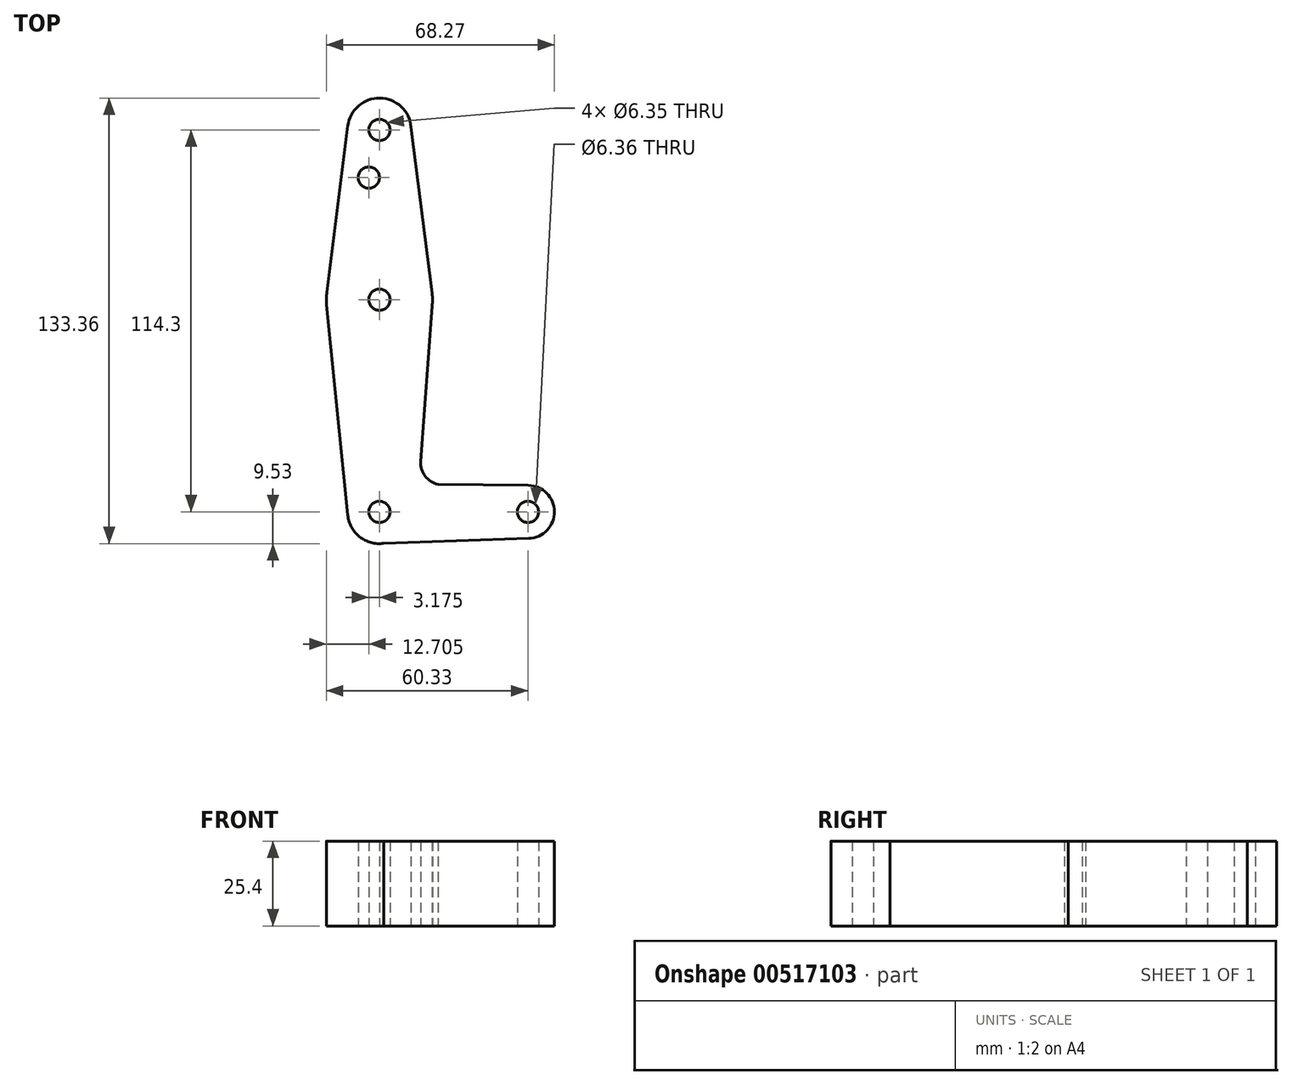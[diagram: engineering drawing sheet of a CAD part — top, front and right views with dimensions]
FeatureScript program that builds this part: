
annotation { "Feature Type Name" : "Feature", "Feature Type Description" : "" }
export const myFeature = defineFeature(function(context is Context, id is Id, definition is map)
    precondition{}
    {
        {
            var Q0;
            Q0=qCreatedBy(makeId("Top.planeOp"),FACE);
            var sketch = newSketch(context, id + "F0", { "sketchPlane" : qUnion([Q0])});
            skCircle(sketch, "E0", {"center": v(0, 0) * mm, "radius": 15.88 * mm});
            skCircle(sketch, "E1", {"center": v(0, 50.8) * mm, "radius": 3.18 * mm});
            skCircle(sketch, "E2", {"center": v(0, 50.8) * mm, "radius": 9.53 * mm});
            skCircle(sketch, "E3", {"center": v(0, 0) * mm, "radius": 3.18 * mm});
            skCircle(sketch, "E4", {"center": v(0, -63.5) * mm, "radius": 3.18 * mm});
            skCircle(sketch, "E5", {"center": v(0, -63.5) * mm, "radius": 9.53 * mm});
            skCircle(sketch, "E6", {"center": v(-3.18, 36.53) * mm, "radius": 3.18 * mm});
            skCircle(sketch, "E7", {"center": v(44.45, -63.5) * mm, "radius": 3.18 * mm});
            skCircle(sketch, "E8", {"center": v(44.45, -63.5) * mm, "radius": 7.94 * mm});
            skLineSegment(sketch, "E9", {"start": v(-9.47, -64.48) * mm, "end": v(-15.95, 0) * mm});
            skLineSegment(sketch, "E10", {"start": v(-15.71, 2.25) * mm, "end": v(-9.45, 52) * mm});
            skLineSegment(sketch, "E11", {"start": v(9.4, 52.32) * mm, "end": v(15.75, 1.99) * mm});
            skLineSegment(sketch, "E12", {"start": v(15.75, -1.99) * mm, "end": v(12.38, -48.36) * mm});
            skArc(sketch, "E13", {"start": v(12.38, -48.36) * mm, "mid": v(13.67, -52.79) * mm, "end": v(17.56, -55.27) * mm});
            skLineSegment(sketch, "E14", {"start": v(17.56, -55.27) * mm, "end": v(44.54, -55.56) * mm});
            skLineSegment(sketch, "E15", {"start": v(44.72, -71.43) * mm, "end": v(0, -72.98) * mm});
            skSolve(sketch);
        }
        {
            var Q0;
            Q0 = qSketchRegion(id + "F0", true);
            extrude(context, id + "F1", {"entities" : qUnion([Q0]), "depth" : 25.4 * mm, "offsetDistance" : 25.4 * mm});
        }
    });
